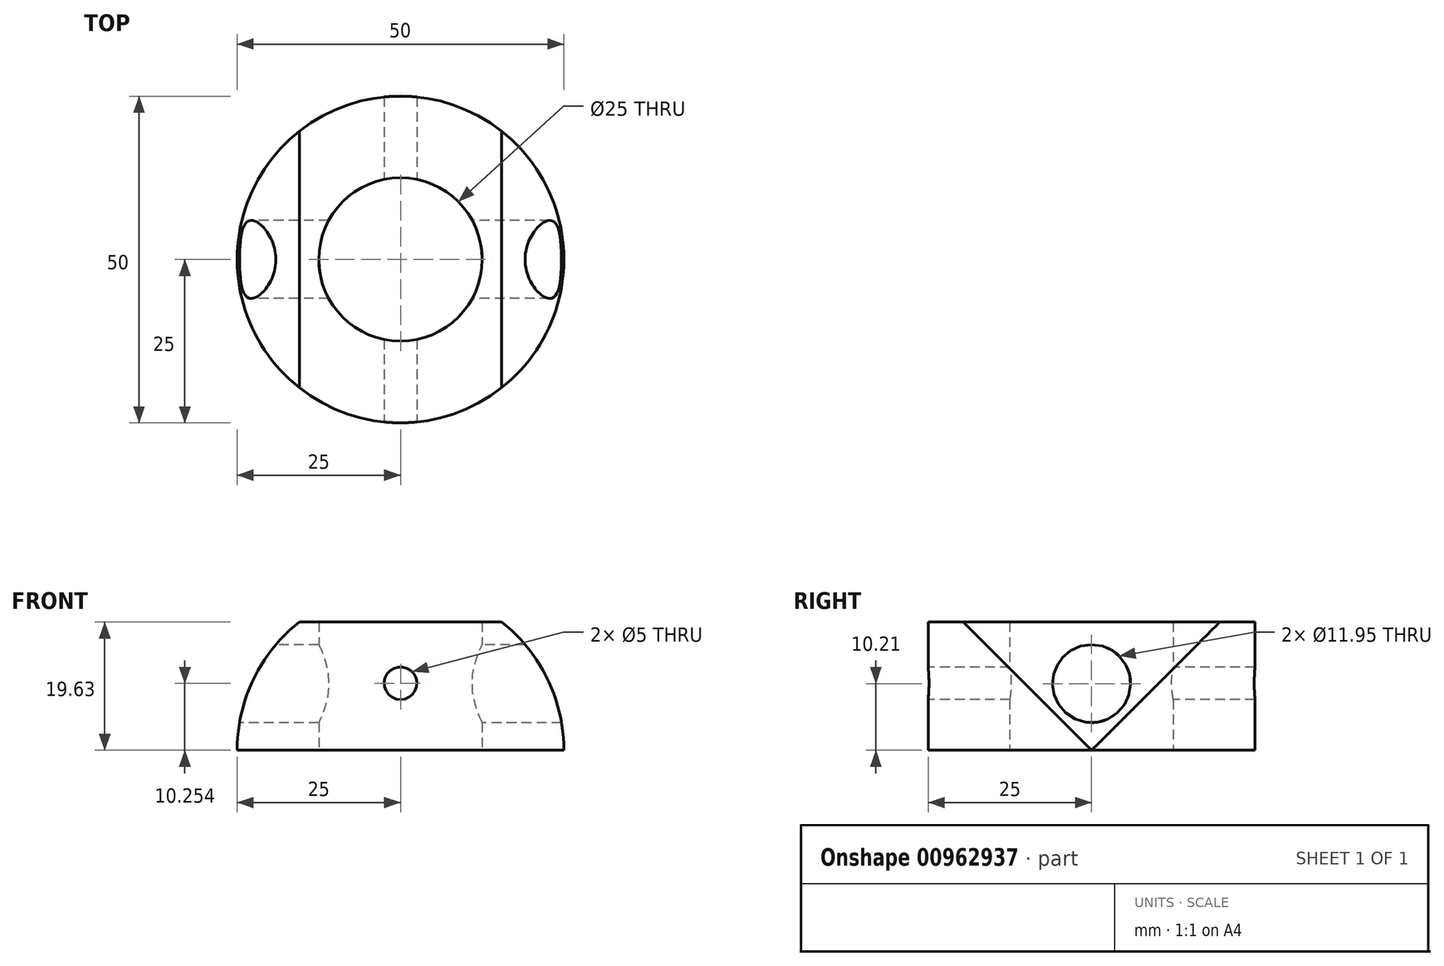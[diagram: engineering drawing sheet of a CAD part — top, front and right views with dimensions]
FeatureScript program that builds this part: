
annotation { "Feature Type Name" : "Feature", "Feature Type Description" : "" }
export const myFeature = defineFeature(function(context is Context, id is Id, definition is map)
    precondition{}
    {
        {
            var Q0;
            Q0=qCreatedBy(makeId("Top.planeOp"),FACE);
            var sketch = newSketch(context, id + "F0", { "sketchPlane" : qUnion([Q0])});
            skCircle(sketch, "E0", {"center": v(0, 0) * mm, "radius": 25 * mm});
            skCircle(sketch, "E1", {"center": v(0, 0) * mm, "radius": 12.5 * mm});
            skSolve(sketch);
        }
        {
            var Q0;
            Q0=qCreatedBy(makeId("Right.planeOp"),FACE);
            var sketch = newSketch(context, id + "F1", { "sketchPlane" : qUnion([Q0])});
            skLineSegment(sketch, "E2.bottom", {"start": v(-25, 0) * mm, "end": v(25, 0) * mm});
            skLineSegment(sketch, "E2.top", {"start": v(-25, 19.63) * mm, "end": v(25, 19.63) * mm});
            skLineSegment(sketch, "E2.left", {"start": v(-25, 0) * mm, "end": v(-25, 19.63) * mm});
            skLineSegment(sketch, "E2.right", {"start": v(25, 0) * mm, "end": v(25, 19.63) * mm});
            skCircle(sketch, "E3", {"center": v(0, 10.21) * mm, "radius": 5.97 * mm});
            skSolve(sketch);
        }
        {
            var Q0;
            Q0=qCreatedBy(makeId("Front.planeOp"),FACE);
            var sketch = newSketch(context, id + "F2", { "sketchPlane" : qUnion([Q0])});
            skCircle(sketch, "E4", {"center": v(0, 0) * mm, "radius": 25 * mm});
            skCircle(sketch, "E5", {"center": v(0, 10.25) * mm, "radius": 2.5 * mm});
            skSolve(sketch);
        }
        {
            var Q0;
            Q0=makeQuery(id+"F0.imprint","IMPRINT",FACE,{"disambiguationData":[TD([[makeQuery(id+"F0.imprint","IMPRINT",EDGE,{"derivedFrom":sQuery(id+"F0.wireOp",EDGE,"E0")}),1.0]])]});
            extrude(context, id + "F3", {"entities" : qUnion([Q0]), "depth" : 50 * mm, "offsetDistance" : 25 * mm});
        }
        {
            var Q0;
            Q0=makeQuery(id+"F1.imprint","IMPRINT",FACE,{"disambiguationData":[TD([[makeQuery(id+"F1.imprint","IMPRINT",EDGE,{"derivedFrom":sQuery(id+"F1.wireOp",EDGE,"E2.bottom")}),1.0]])]});
            extrude(context, id + "F4", {"entities" : qUnion([Q0]), "endBound" : BoundingType.SYMMETRIC, "depth" : 50 * mm, "offsetDistance" : 25 * mm});
        }
        {
            var Q0;
            Q0=makeQuery(id+"F2.imprint","IMPRINT",FACE,{"disambiguationData":[TD([[makeQuery(id+"F2.imprint","IMPRINT",EDGE,{"derivedFrom":sQuery(id+"F2.wireOp",EDGE,"E4")}),1.0]])]});
            extrude(context, id + "F5", {"entities" : qUnion([Q0]), "endBound" : BoundingType.SYMMETRIC, "oppositeDirection" : true, "depth" : 50 * mm, "offsetDistance" : 25 * mm});
        }
        {
            var Q0;
            Q0=makeQuery(id+"F3.opExtrude","SWEPT_BODY",BODY,{"disambiguationData":[OSD([sQuery(id+"F0.wireOp",EDGE,"E0")])]});
            var Q1;
            Q1=makeQuery(id+"F4.opExtrude","SWEPT_BODY",BODY,{"disambiguationData":[OSD([sQuery(id+"F1.wireOp",EDGE,"E2.bottom"),sQuery(id+"F1.wireOp",EDGE,"E2.top"),sQuery(id+"F1.wireOp",EDGE,"E2.left"),sQuery(id+"F1.wireOp",EDGE,"E2.right")])]});
            var Q2;
            Q2=makeQuery(id+"F5.opExtrude","SWEPT_BODY",BODY,{"disambiguationData":[OSD([sQuery(id+"F2.wireOp",EDGE,"E4"),sQuery(id+"F2.wireOp",EDGE,"E5")])]});
            booleanBodies(context, id + "F6", {"operationType" : BooleanOperationType.INTERSECTION, "tools" : qUnion([Q0, Q1, Q2])});
        }
    });
